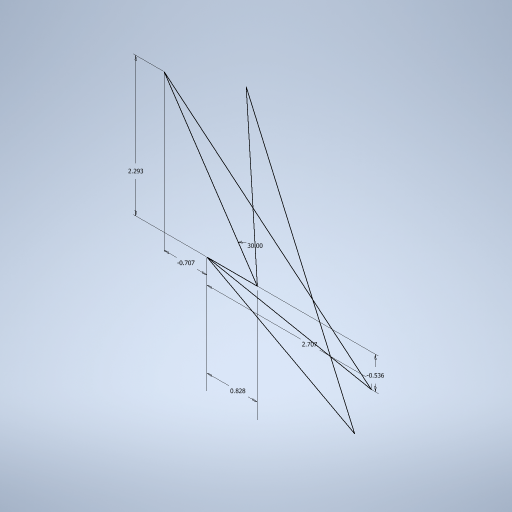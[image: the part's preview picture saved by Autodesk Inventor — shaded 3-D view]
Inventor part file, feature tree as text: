
AUTODESK INVENTOR PART (.ipt)
format: ipt  version: 2024 (Build 280153000, 153)  size: 241,152 bytes
history: native  units: in
note: dims shown in document units (in); Inventor stores cm internally (conversion verified against a paired STEP export)
features: sketch x1
ambient origin geometry x8: Origin, YZ Plane, XZ Plane, XY Plane, X Axis, Y Axis, Z Axis, Center Point
feature tree (1):
  sketch  "Sketch1"  dims[d0=0.0326in d1=-0.0278in d2=0.0903in d3=0.1066in d4=-0.0211in d5=30.0deg]
